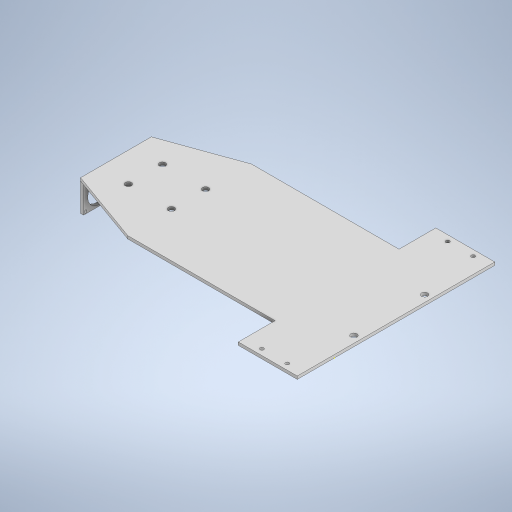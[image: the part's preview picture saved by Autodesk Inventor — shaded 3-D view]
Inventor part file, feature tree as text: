
AUTODESK INVENTOR PART (.ipt)
format: ipt  version: 2024.2 (Build 282272000, 272)  size: 335,360 bytes
history: native  units: mm
features: sketch x4, extrude x3, other x1
ambient origin geometry x8: Origin, YZ Plane, XZ Plane, XY Plane, X Axis, Y Axis, Z Axis, Center Point
bodies: Body1 (feature_tree)
feature tree (8):
  other  "Bryła1"
  sketch  "Szkic1"
  extrude  "Wyciągnięcie proste1"  Depth=48.0mm
  extrude  "Wyciągnięcie proste2"  Depth=140.0mm
  extrude  "Wyciągnięcie proste3"  Depth=84.0mm
  sketch  "Szkic2"
  sketch  "Szkic3"
  sketch  "Szkic4"
